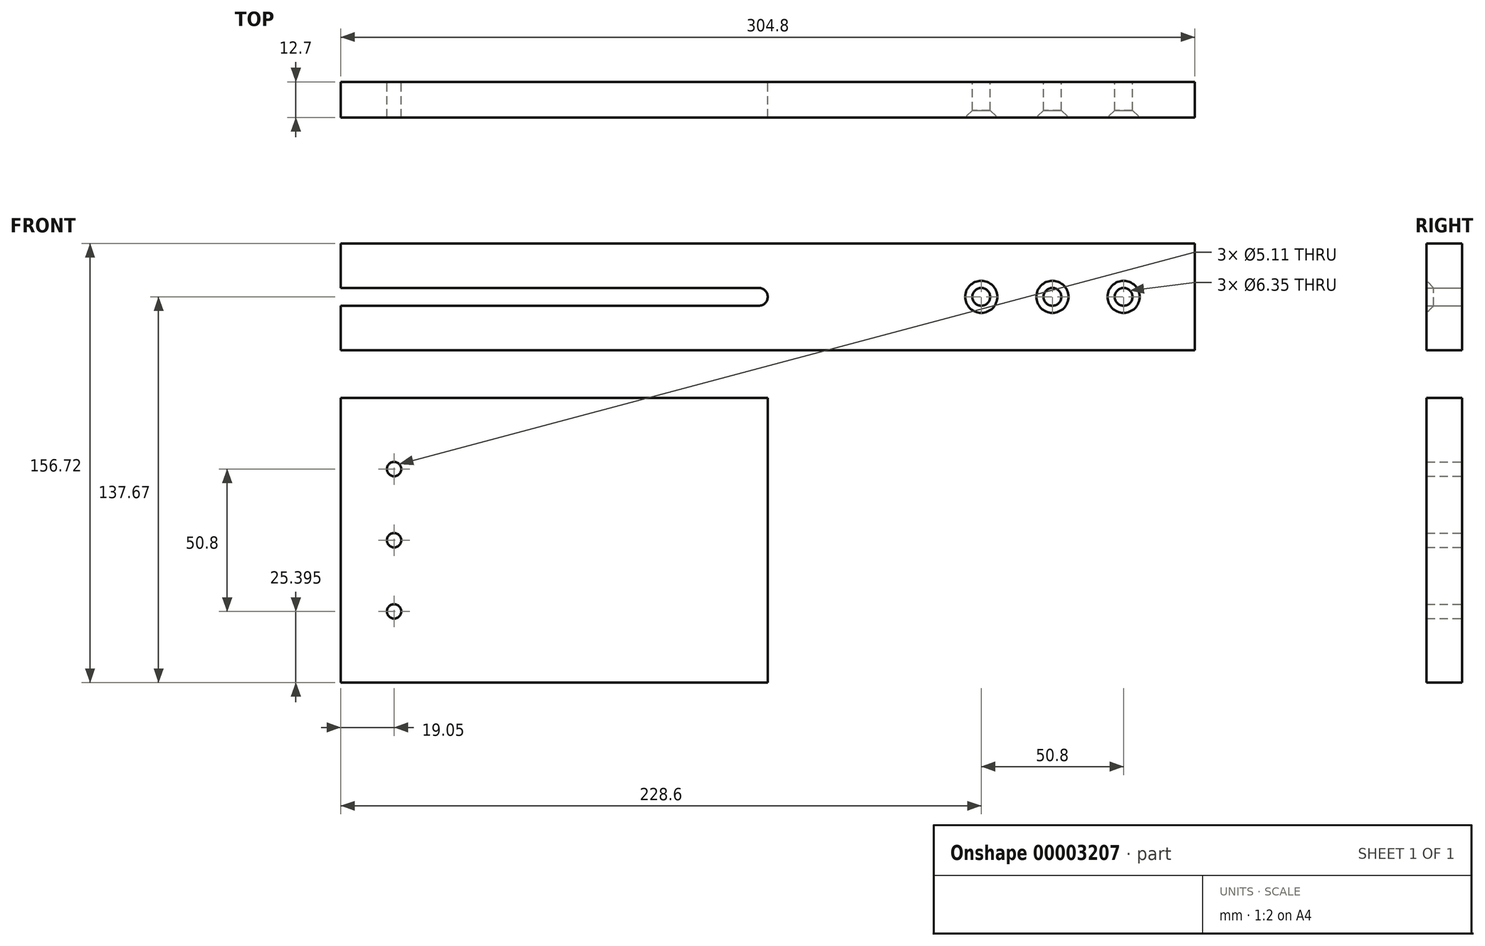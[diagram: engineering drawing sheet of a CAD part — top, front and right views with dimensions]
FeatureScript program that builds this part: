
annotation { "Feature Type Name" : "Feature", "Feature Type Description" : "" }
export const myFeature = defineFeature(function(context is Context, id is Id, definition is map)
    precondition{}
    {
        {
            var Q0;
            Q0=qCreatedBy(makeId("Front.planeOp"),FACE);
            var sketch = newSketch(context, id + "F0", { "sketchPlane" : qUnion([Q0])});
            skLineSegment(sketch, "E0", {"start": v(0, 0) * mm, "end": v(0, -38.1) * mm});
            skLineSegment(sketch, "E1", {"start": v(0, -38.1) * mm, "end": v(304.8, -38.1) * mm});
            skLineSegment(sketch, "E2", {"start": v(304.8, -38.1) * mm, "end": v(304.8, 0) * mm});
            skLineSegment(sketch, "E3", {"start": v(304.8, 0) * mm, "end": v(0, 0) * mm});
            skLineSegment(sketch, "E4", {"start": v(279.4, 0) * mm, "end": v(279.4, -38.1) * mm, "construction": true});
            skLineSegment(sketch, "E5", {"start": v(254, 0) * mm, "end": v(254, -38.1) * mm, "construction": true});
            skLineSegment(sketch, "E6", {"start": v(228.6, 0) * mm, "end": v(228.6, -38.1) * mm, "construction": true});
            skCircle(sketch, "E7", {"center": v(228.6, -19.05) * mm, "radius": 3.18 * mm});
            skCircle(sketch, "E8", {"center": v(254, -19.05) * mm, "radius": 3.18 * mm});
            skCircle(sketch, "E9", {"center": v(279.4, -19.05) * mm, "radius": 3.18 * mm});
            skLineSegment(sketch, "E10", {"start": v(152.4, 0) * mm, "end": v(152.4, -38.1) * mm, "construction": true});
            skLineSegment(sketch, "E11", {"start": v(0, -15.88) * mm, "end": v(152.4, -15.87) * mm});
            skLineSegment(sketch, "E12", {"start": v(0, -22.23) * mm, "end": v(152.4, -22.23) * mm});
            skLineSegment(sketch, "E13", {"start": v(152.4, -15.87) * mm, "end": v(152.4, -22.23) * mm});
            skArc(sketch, "E14", {"start": v(149.22, -22.23) * mm, "mid": v(151.47, -21.3) * mm, "end": v(152.4, -19.05) * mm});
            skArc(sketch, "E15", {"start": v(152.4, -19.05) * mm, "mid": v(151.47, -16.8) * mm, "end": v(149.22, -15.87) * mm});
            skSolve(sketch);
        }
        {
            var Q0;
            {var subQ14=sQuery(id+"F0.wireOp",EDGE,"E1");Q0=makeQuery(id+"F0.imprint","IMPRINT",FACE,{"disambiguationData":[TD([[makeQuery(id+"F0.imprint","IMPRINT",EDGE,{"derivedFrom":subQ14}),1.0]])]});}
            var Q1;
            {var subQ0=sQuery(id+"F0.wireOp",EDGE,"E15");Q1=makeQuery(id+"F0.imprint","IMPRINT",FACE,{"disambiguationData":[TD([[makeQuery(id+"F0.imprint","IMPRINT",EDGE,{"derivedFrom":subQ0}),-1.0]])]});}
            var Q2;
            {var subQ0=sQuery(id+"F0.wireOp",EDGE,"E14");Q2=makeQuery(id+"F0.imprint","IMPRINT",FACE,{"disambiguationData":[TD([[makeQuery(id+"F0.imprint","IMPRINT",EDGE,{"derivedFrom":subQ0}),-1.0]])]});}
            extrude(context, id + "F1", {"entities" : qUnion([Q0, Q1, Q2]), "endBound" : BoundingType.SYMMETRIC, "depth" : 12.7 * mm});
        }
        {
            var Q0;
            Q0=qCreatedBy(makeId("Front.planeOp"),FACE);
            var sketch = newSketch(context, id + "F2", { "sketchPlane" : qUnion([Q0])});
            skLineSegment(sketch, "E16", {"start": v(0, -55.12) * mm, "end": v(0, -156.72) * mm});
            skLineSegment(sketch, "E17", {"start": v(0, -156.72) * mm, "end": v(152.4, -156.72) * mm});
            skLineSegment(sketch, "E18", {"start": v(152.4, -156.72) * mm, "end": v(152.4, -55.12) * mm});
            skLineSegment(sketch, "E19", {"start": v(152.4, -55.12) * mm, "end": v(0, -55.12) * mm});
            skLineSegment(sketch, "E20", {"start": v(19.05, -55.12) * mm, "end": v(19.05, -156.72) * mm, "construction": true});
            skLineSegment(sketch, "E21", {"start": v(0, -80.52) * mm, "end": v(152.4, -80.52) * mm, "construction": true});
            skLineSegment(sketch, "E22", {"start": v(0, -105.92) * mm, "end": v(152.4, -105.92) * mm, "construction": true});
            skLineSegment(sketch, "E23", {"start": v(0, -131.32) * mm, "end": v(152.4, -131.32) * mm, "construction": true});
            skCircle(sketch, "E24", {"center": v(19.05, -80.52) * mm, "radius": 2.55 * mm});
            skCircle(sketch, "E25", {"center": v(19.05, -105.92) * mm, "radius": 2.55 * mm});
            skCircle(sketch, "E26", {"center": v(19.05, -131.32) * mm, "radius": 2.55 * mm});
            skSolve(sketch);
        }
        {
            var Q0;
            Q0 = qSketchRegion(id + "F2", true);
            extrude(context, id + "F3", {"entities" : qUnion([Q0]), "endBound" : BoundingType.SYMMETRIC, "depth" : 12.7 * mm});
        }
        {
            var Q0;
            Q0=makeQuery(id+"F1.opExtrude","CAP_EDGE",EDGE,{"disambiguationData":[OSD([sQuery(id+"F0.wireOp",EDGE,"E7")])],"isStart":false});
            var Q1;
            Q1=makeQuery(id+"F1.opExtrude","CAP_EDGE",EDGE,{"disambiguationData":[OSD([sQuery(id+"F0.wireOp",EDGE,"E8")])],"isStart":false});
            var Q2;
            Q2=makeQuery(id+"F1.opExtrude","CAP_EDGE",EDGE,{"disambiguationData":[OSD([sQuery(id+"F0.wireOp",EDGE,"E9")])],"isStart":false});
            chamfer(context, id + "F4", {"entities" : qUnion([Q0, Q1, Q2]), "chamferType" : ChamferType.OFFSET_ANGLE, "width" : 2.54 * mm, "oppositeDirection" : false, "angle" : 45 * degree, "tangentPropagation" : true});
        }
    });
